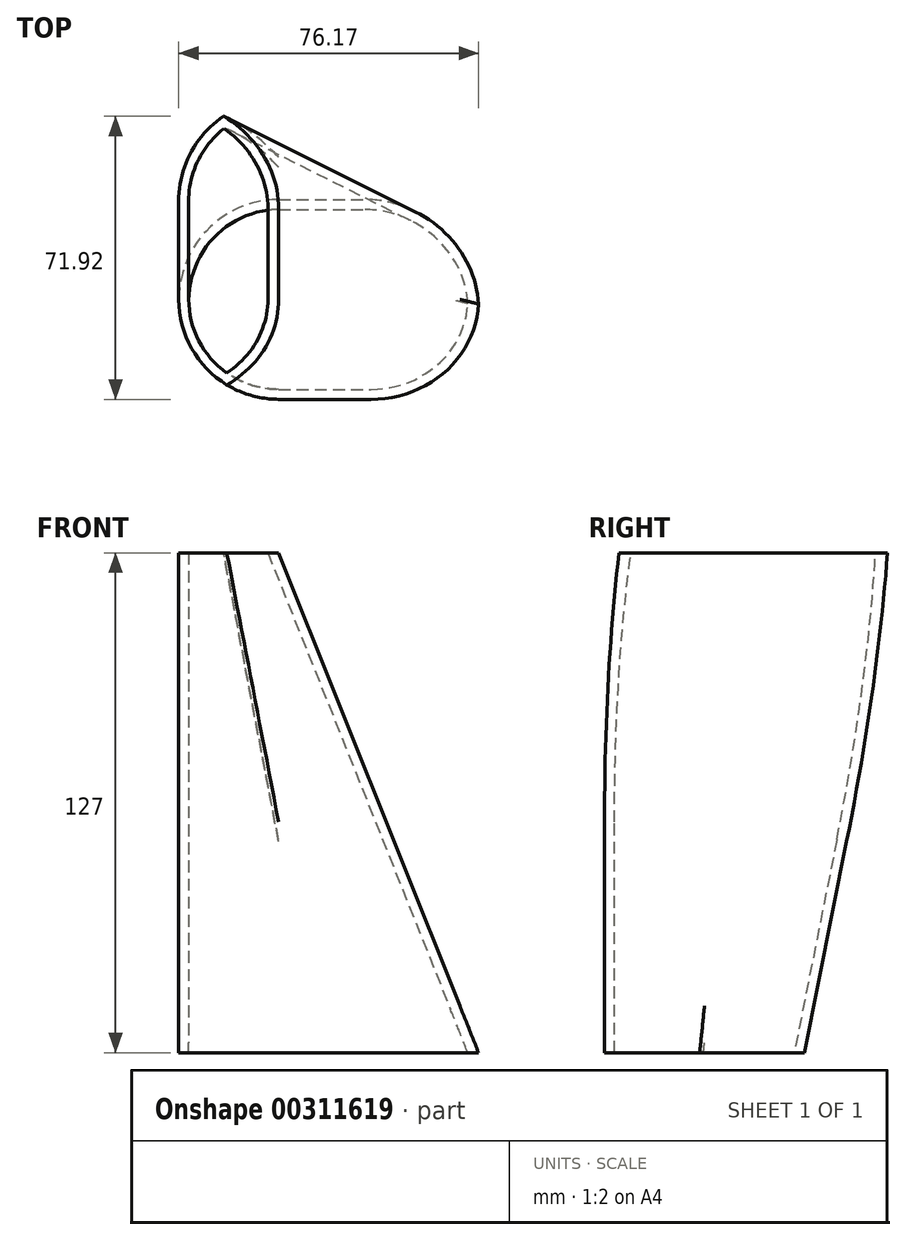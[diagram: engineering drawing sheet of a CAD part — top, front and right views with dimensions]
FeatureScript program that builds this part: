
annotation { "Feature Type Name" : "Feature", "Feature Type Description" : "" }
export const myFeature = defineFeature(function(context is Context, id is Id, definition is map)
    precondition{}
    {
        {
            var Q0;
            Q0=qCreatedBy(makeId("Top.planeOp"),FACE);
            var sketch = newSketch(context, id + "F0", { "sketchPlane" : qUnion([Q0])});
            skLineSegment(sketch, "E0.bottom", {"start": v(0, 0) * mm, "end": v(76.2, 0) * mm});
            skLineSegment(sketch, "E0.top", {"start": v(0, 50.8) * mm, "end": v(76.2, 50.8) * mm});
            skLineSegment(sketch, "E0.left", {"start": v(0, 0) * mm, "end": v(0, 50.8) * mm});
            skLineSegment(sketch, "E0.right", {"start": v(76.2, 0) * mm, "end": v(76.2, 50.8) * mm});
            skSolve(sketch);
        }
        {
            var Q0;
            Q0=qCreatedBy(makeId("Top.planeOp"),FACE);
            cPlane(context, id + "F1", {"entities" : qUnion([Q0]), "cplaneType" : CPlaneType.OFFSET, "offset" : 127 * mm, "width" : 152.4 * mm, "height" : 152.4 * mm});
        }
        {
            var Q0;
            Q0=qCreatedBy(id+"F1.planeOp",FACE);
            var sketch = newSketch(context, id + "F2", { "sketchPlane" : qUnion([Q0])});
            skLineSegment(sketch, "E1.bottom", {"start": v(0, 0) * mm, "end": v(25.4, 0) * mm});
            skLineSegment(sketch, "E1.top", {"start": v(0, 76.2) * mm, "end": v(25.4, 76.2) * mm});
            skLineSegment(sketch, "E1.left", {"start": v(0, 0) * mm, "end": v(0, 76.2) * mm});
            skLineSegment(sketch, "E1.right", {"start": v(25.4, 0) * mm, "end": v(25.4, 76.2) * mm});
            skSolve(sketch);
        }
        {
            var Q0;
            Q0=makeQuery(id+"F0.imprint","IMPRINT",FACE,{"disambiguationData":[TD([[makeQuery(id+"F0.imprint","IMPRINT",EDGE,{"derivedFrom":sQuery(id+"F0.wireOp",EDGE,"E0.bottom")}),1.0]])]});
            var Q1;
            Q1=makeQuery(id+"F2.imprint","IMPRINT",FACE,{"disambiguationData":[TD([[makeQuery(id+"F2.imprint","IMPRINT",EDGE,{"derivedFrom":sQuery(id+"F2.wireOp",EDGE,"E1.bottom")}),1.0]])]});
            loft(context, id + "F3", {"sheetProfilesArray" : [{ "sheetProfileEntities" : qUnion([Q0]) }, { "sheetProfileEntities" : qUnion([Q1]) }]});
        }
        {
            var Q0;
            Q0=makeQuery(id+"F3.opLoft","SWEPT_EDGE",EDGE,{"disambiguationData":[OSD([sQuery(id+"F0.wireOp",EDGE,"E0.bottom"),sQuery(id+"F0.wireOp",EDGE,"E0.right"),sQuery(id+"F2.wireOp",EDGE,"E1.bottom"),sQuery(id+"F2.wireOp",EDGE,"E1.right")])]});
            var Q1;
            Q1=makeQuery(id+"F3.opLoft","SWEPT_EDGE",EDGE,{"disambiguationData":[OSD([sQuery(id+"F0.wireOp",EDGE,"E0.bottom"),sQuery(id+"F0.wireOp",EDGE,"E0.left"),sQuery(id+"F2.wireOp",EDGE,"E1.bottom"),sQuery(id+"F2.wireOp",EDGE,"E1.left")])]});
            var Q2;
            Q2=makeQuery(id+"F3.opLoft","SWEPT_EDGE",EDGE,{"disambiguationData":[OSD([sQuery(id+"F0.wireOp",EDGE,"E0.top"),sQuery(id+"F0.wireOp",EDGE,"E0.right"),sQuery(id+"F2.wireOp",EDGE,"E1.top"),sQuery(id+"F2.wireOp",EDGE,"E1.right")])]});
            var Q3;
            Q3=makeQuery(id+"F3.opLoft","SWEPT_EDGE",EDGE,{"disambiguationData":[OSD([sQuery(id+"F0.wireOp",EDGE,"E0.top"),sQuery(id+"F0.wireOp",EDGE,"E0.left"),sQuery(id+"F2.wireOp",EDGE,"E1.top"),sQuery(id+"F2.wireOp",EDGE,"E1.left")])]});
            fillet(context, id + "F4", {"entities" : qUnion([Q0, Q1, Q2, Q3]), "radius" : 25.4 * mm, "tangentPropagation" : true, "allowEdgeOverflow" : false});
        }
        {
            var Q0;
            Q0=makeQuery(id+"F3.opLoft","CAP_FACE",FACE,{"disambiguationData":[OSD([makeQuery(id+"F2.imprint","IMPRINT",FACE,{"disambiguationData":[TD([[makeQuery(id+"F2.imprint","IMPRINT",EDGE,{"derivedFrom":sQuery(id+"F2.wireOp",EDGE,"E1.bottom")}),1.0]])]})])],"isStart":true});
            var Q1;
            Q1=makeQuery(id+"F3.opLoft","CAP_FACE",FACE,{"disambiguationData":[OSD([makeQuery(id+"F0.imprint","IMPRINT",FACE,{"disambiguationData":[TD([[makeQuery(id+"F0.imprint","IMPRINT",EDGE,{"derivedFrom":sQuery(id+"F0.wireOp",EDGE,"E0.bottom")}),1.0]])]})])],"isStart":true});
            shell(context, id + "F5", {"entities" : qUnion([Q0, Q1]), "thickness" : 2.54 * mm});
        }
    });
